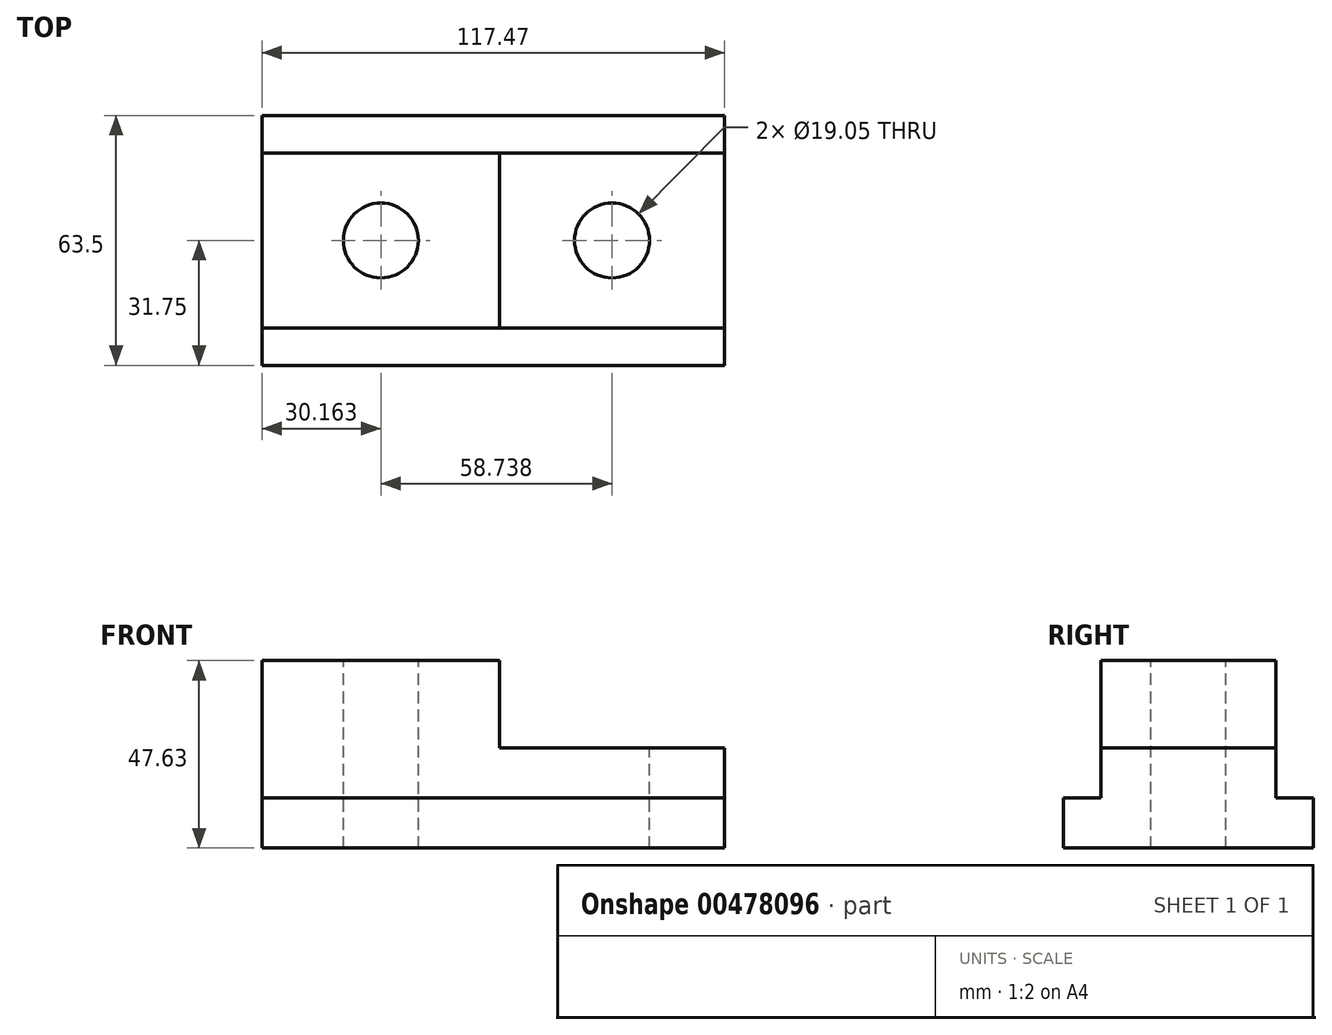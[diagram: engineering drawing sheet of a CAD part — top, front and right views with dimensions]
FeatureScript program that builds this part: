
annotation { "Feature Type Name" : "Feature", "Feature Type Description" : "" }
export const myFeature = defineFeature(function(context is Context, id is Id, definition is map)
    precondition{}
    {
        {
            var Q0;
            Q0=qCreatedBy(makeId("Right.planeOp"),FACE);
            var sketch = newSketch(context, id + "F0", { "sketchPlane" : qUnion([Q0])});
            skLineSegment(sketch, "E0", {"start": v(0, 0) * mm, "end": v(63.5, 0) * mm});
            skLineSegment(sketch, "E1", {"start": v(63.5, 0) * mm, "end": v(63.5, 12.7) * mm});
            skLineSegment(sketch, "E2", {"start": v(63.5, 12.7) * mm, "end": v(53.97, 12.7) * mm});
            skLineSegment(sketch, "E3", {"start": v(53.97, 12.7) * mm, "end": v(53.97, 47.63) * mm});
            skLineSegment(sketch, "E4", {"start": v(53.97, 47.63) * mm, "end": v(9.52, 47.62) * mm});
            skLineSegment(sketch, "E5", {"start": v(9.52, 47.62) * mm, "end": v(9.52, 12.7) * mm});
            skLineSegment(sketch, "E6", {"start": v(9.52, 12.7) * mm, "end": v(0, 12.7) * mm});
            skLineSegment(sketch, "E7", {"start": v(0, 12.7) * mm, "end": v(0, 0) * mm});
            skSolve(sketch);
        }
        {
            var Q0;
            Q0=makeQuery(id+"F0.imprint","IMPRINT",FACE,{"disambiguationData":[TD([[makeQuery(id+"F0.imprint","IMPRINT",EDGE,{"derivedFrom":sQuery(id+"F0.wireOp",EDGE,"E0")}),1.0]])]});
            extrude(context, id + "F1", {"entities" : qUnion([Q0]), "depth" : 117.47 * mm});
        }
        {
            var Q0;
            Q0=makeQuery(id+"F1.opExtrude","SWEPT_FACE",FACE,{"disambiguationData":[OSD([sQuery(id+"F0.wireOp",EDGE,"E4")])]});
            var sketch = newSketch(context, id + "F2", { "sketchPlane" : qUnion([Q0])});
            skLineSegment(sketch, "E8", {"start": v(0, 53.97) * mm, "end": v(60.33, 53.97) * mm, "construction": true});
            skLineSegment(sketch, "E9", {"start": v(60.33, 53.97) * mm, "end": v(60.33, 9.53) * mm, "construction": true});
            skLineSegment(sketch, "E10", {"start": v(60.33, 9.52) * mm, "end": v(0, 9.52) * mm, "construction": true});
            skLineSegment(sketch, "E11", {"start": v(0, 9.52) * mm, "end": v(0, 53.97) * mm, "construction": true});
            skLineSegment(sketch, "E12", {"start": v(0, 53.97) * mm, "end": v(30.16, 53.97) * mm, "construction": true});
            skLineSegment(sketch, "E13", {"start": v(60.33, 53.97) * mm, "end": v(117.48, 53.98) * mm, "construction": true});
            skLineSegment(sketch, "E14", {"start": v(0, 31.75) * mm, "end": v(117.48, 31.75) * mm, "construction": true});
            skLineSegment(sketch, "E15", {"start": v(30.16, 53.97) * mm, "end": v(30.16, 9.52) * mm, "construction": true});
            skLineSegment(sketch, "E16", {"start": v(88.9, 53.97) * mm, "end": v(88.9, 9.52) * mm, "construction": true});
            skCircle(sketch, "E17", {"center": v(30.16, 31.75) * mm, "radius": 9.53 * mm});
            skCircle(sketch, "E18", {"center": v(88.9, 31.75) * mm, "radius": 9.53 * mm});
            skSolve(sketch);
        }
        {
            var Q0;
            Q0=makeQuery(id+"F2.imprint","IMPRINT",FACE,{"disambiguationData":[TD([[makeQuery(id+"F2.imprint","IMPRINT",EDGE,{"derivedFrom":sQuery(id+"F2.wireOp",EDGE,"E17")}),1.0]])]});
            var Q1;
            Q1=makeQuery(id+"F2.imprint","IMPRINT",FACE,{"disambiguationData":[TD([[makeQuery(id+"F2.imprint","IMPRINT",EDGE,{"derivedFrom":sQuery(id+"F2.wireOp",EDGE,"E18")}),1.0]])]});
            extrude(context, id + "F3", {"entities" : qUnion([Q0, Q1]), "operationType" : NewBodyOperationType.REMOVE, "oppositeDirection" : true, "depth" : 161.29 * mm});
        }
        {
            var Q0;
            Q0=makeQuery(id+"F1.opExtrude","CAP_FACE",FACE,{"disambiguationData":[OSD([sQuery(id+"F0.wireOp",EDGE,"E0"),sQuery(id+"F0.wireOp",EDGE,"E1"),sQuery(id+"F0.wireOp",EDGE,"E2"),sQuery(id+"F0.wireOp",EDGE,"E3"),sQuery(id+"F0.wireOp",EDGE,"E4"),sQuery(id+"F0.wireOp",EDGE,"E5"),sQuery(id+"F0.wireOp",EDGE,"E6"),sQuery(id+"F0.wireOp",EDGE,"E7")])],"isStart":false});
            var sketch = newSketch(context, id + "F4", { "sketchPlane" : qUnion([Q0])});
            skLineSegment(sketch, "E19", {"start": v(9.52, 0) * mm, "end": v(9.52, 25.4) * mm, "construction": true});
            skLineSegment(sketch, "E20.bottom", {"start": v(9.52, 25.4) * mm, "end": v(53.97, 25.4) * mm});
            skLineSegment(sketch, "E20.top", {"start": v(9.52, 47.63) * mm, "end": v(53.97, 47.63) * mm});
            skLineSegment(sketch, "E20.left", {"start": v(9.52, 25.4) * mm, "end": v(9.52, 47.63) * mm});
            skLineSegment(sketch, "E20.right", {"start": v(53.97, 25.4) * mm, "end": v(53.97, 47.63) * mm});
            skSolve(sketch);
        }
        {
            var Q0;
            Q0=makeQuery(id+"F4.imprint","IMPRINT",FACE,{"disambiguationData":[TD([[makeQuery(id+"F4.imprint","IMPRINT",EDGE,{"derivedFrom":sQuery(id+"F4.wireOp",EDGE,"E20.bottom")}),1.0]])]});
            extrude(context, id + "F5", {"entities" : qUnion([Q0]), "operationType" : NewBodyOperationType.REMOVE, "oppositeDirection" : true, "depth" : 57.15 * mm});
        }
    });
